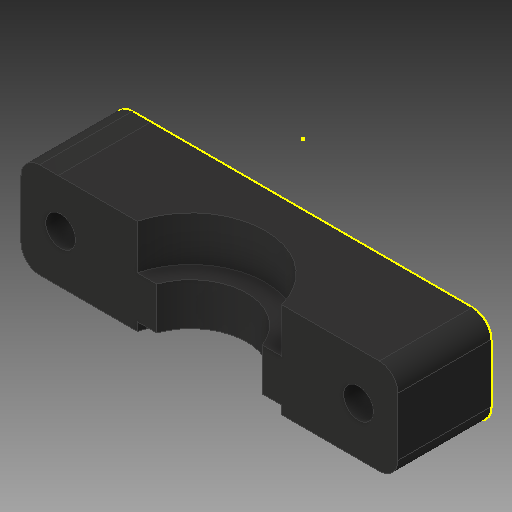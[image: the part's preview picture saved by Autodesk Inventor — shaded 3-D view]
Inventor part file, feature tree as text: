
AUTODESK INVENTOR PART (.ipt)
format: ipt  version: 2018 (Build 220112000, 112)  size: 163,840 bytes
history: native  units: in
note: dims shown in document units (in); Inventor stores cm internally (conversion verified against a paired STEP export)
features: sketch x5, extrude x4, other x3, reference x1, projected_geometry x1
ambient origin geometry x8: Origin, YZ Plane, XZ Plane, XY Plane, X Axis, Y Axis, Z Axis, Center Point
bodies: Solid1 (feature_tree)
feature tree (14):
  extrude  "Extrusion1"  Depth=0.0787in
  extrude  "Extrusion2"  Depth=0.0787in
  extrude  "Extrusion3"  Depth=0.189in TaperAngle=0.0deg
  extrude  "Extrusion4"  Depth=0.189in TaperAngle=0.0deg
  sketch  "Sketch5"  dims[d12=0.6299in d13=0.0354in d14=0.0in]
  sketch  "Sketch1"  dims[d1=0.0787in d2=0.0787in]
  reference  "Reference1"
  sketch  "Sketch2"  dims[d3=0.3937in d4=0.0in d5=0.0787in]
  sketch  "Sketch3"  dims[d6=0.6299in d7=0.189in d8=0.0in]
  sketch  "Sketch4"  dims[d9=0.4724in d10=0.189in d11=0.0in]
  projected_geometry  "Projected Loop1"
  other  "<userpath>\OneDrive\Inventor\Beast 3D Printer\Hotend Mount Assembly.iam"
  other  "Hotend Mount Assembly.iam"
  other  "Hotend Slide Part 1:1"
